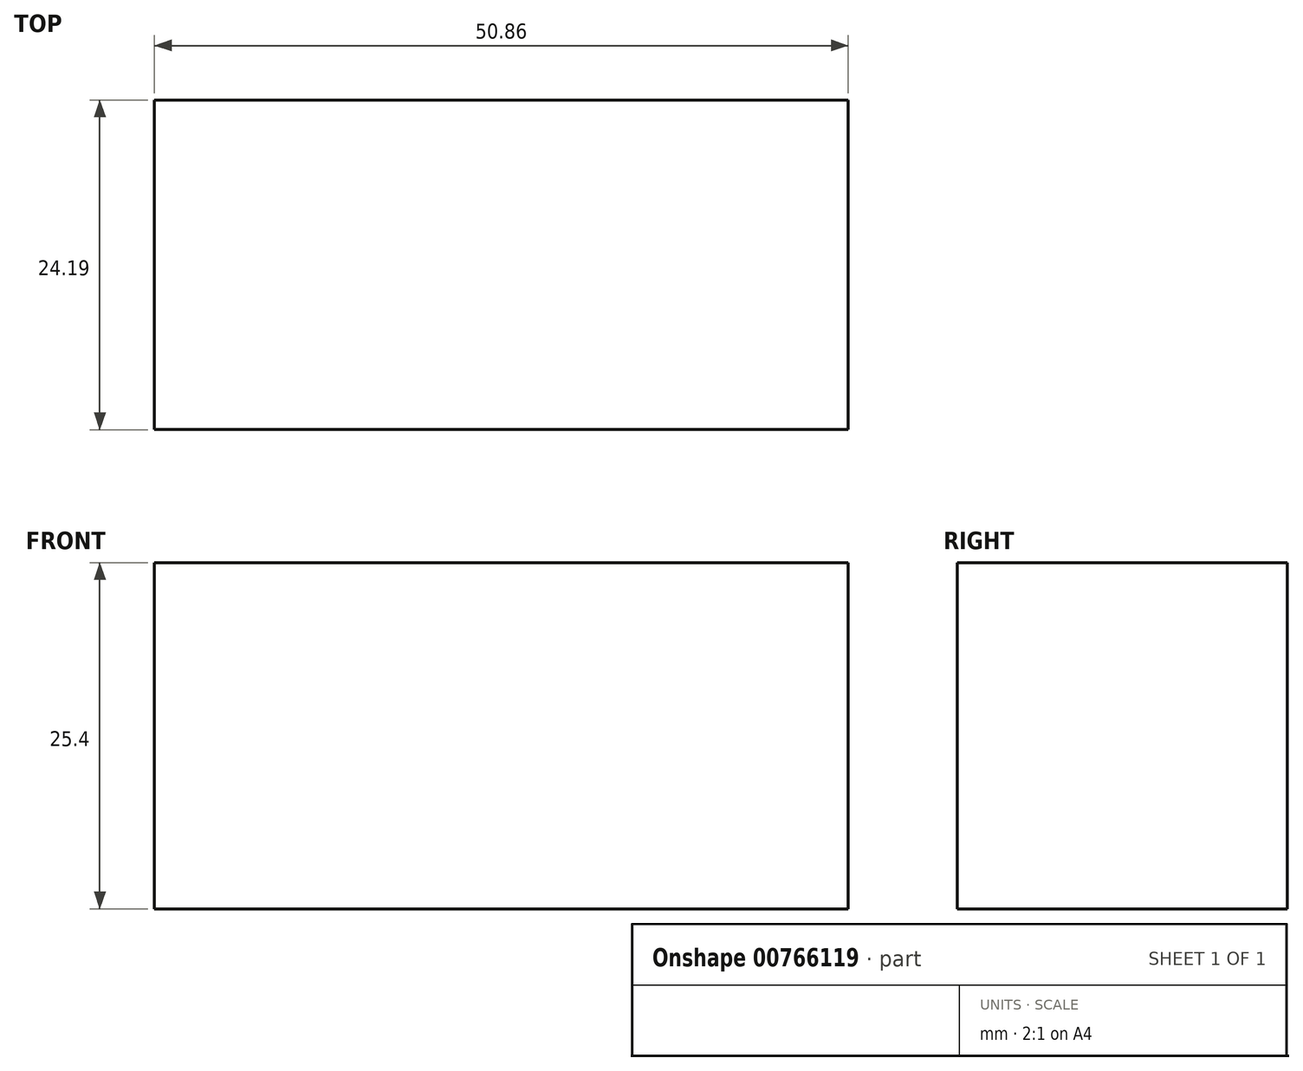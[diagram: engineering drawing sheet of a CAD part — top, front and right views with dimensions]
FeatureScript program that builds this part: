
annotation { "Feature Type Name" : "Feature", "Feature Type Description" : "" }
export const myFeature = defineFeature(function(context is Context, id is Id, definition is map)
    precondition{}
    {
        {
            var Q0;
            Q0=qCreatedBy(makeId("Top.planeOp"),FACE);
            var sketch = newSketch(context, id + "F0", { "sketchPlane" : qUnion([Q0])});
            skLineSegment(sketch, "E0.bottom", {"start": v(25.43, 35.93) * mm, "end": v(-25.43, 35.93) * mm});
            skLineSegment(sketch, "E0.top", {"start": v(25.43, 60.12) * mm, "end": v(-25.43, 60.12) * mm});
            skLineSegment(sketch, "E0.left", {"start": v(25.43, 35.93) * mm, "end": v(25.43, 60.12) * mm});
            skLineSegment(sketch, "E0.right", {"start": v(-25.43, 35.93) * mm, "end": v(-25.43, 60.12) * mm});
            skPoint(sketch, "E0.middle", {"position": v(0, 48.03) * mm});
            skSolve(sketch);
        }
        {
            var Q0;
            Q0=makeQuery(id+"F0.imprint","IMPRINT",FACE,{"disambiguationData":[TD([[makeQuery(id+"F0.imprint","IMPRINT",EDGE,{"derivedFrom":sQuery(id+"F0.wireOp",EDGE,"E0.bottom")}),-1.0]])]});
            extrude(context, id + "F1", {"entities" : qUnion([Q0]), "depth" : 25.4 * mm, "offsetDistance" : 25.4 * mm});
        }
    });
